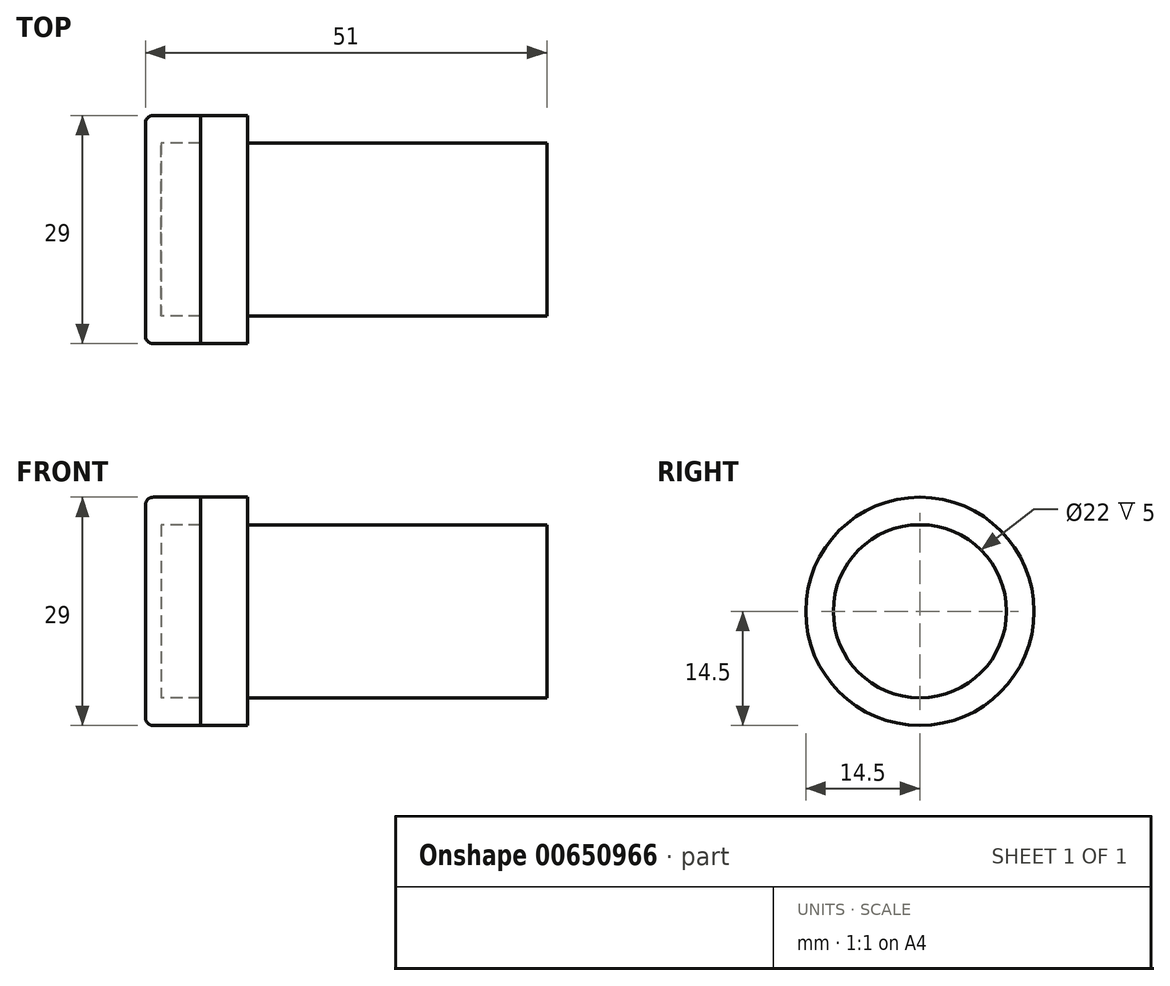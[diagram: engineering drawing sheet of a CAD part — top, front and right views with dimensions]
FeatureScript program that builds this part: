
annotation { "Feature Type Name" : "Feature", "Feature Type Description" : "" }
export const myFeature = defineFeature(function(context is Context, id is Id, definition is map)
    precondition{}
    {
        {
            var Q0;
            Q0=qCreatedBy(makeId("Top.planeOp"),FACE);
            var sketch = newSketch(context, id + "F0", { "sketchPlane" : qUnion([Q0])});
            skLineSegment(sketch, "E0", {"start": v(51, 0) * mm, "end": v(51, 11) * mm});
            skLineSegment(sketch, "E1", {"start": v(51, 11) * mm, "end": v(13, 11) * mm});
            skLineSegment(sketch, "E2", {"start": v(13, 11) * mm, "end": v(13, 14.5) * mm});
            skLineSegment(sketch, "E3", {"start": v(13, 14.5) * mm, "end": v(7, 14.5) * mm});
            skLineSegment(sketch, "E4", {"start": v(7, 14.5) * mm, "end": v(7, 11) * mm});
            skLineSegment(sketch, "E5", {"start": v(0, 11) * mm, "end": v(0, 0) * mm});
            skLineSegment(sketch, "E6", {"start": v(0, 11) * mm, "end": v(0, 14.5) * mm});
            skLineSegment(sketch, "E7", {"start": v(0, 14.5) * mm, "end": v(7, 14.5) * mm});
            skLineSegment(sketch, "E8", {"start": v(2, 0) * mm, "end": v(2, 11) * mm});
            skLineSegment(sketch, "E9", {"start": v(0, 11) * mm, "end": v(2, 11) * mm});
            skLineSegment(sketch, "E10", {"start": v(2, 11) * mm, "end": v(7, 11) * mm});
            skLineSegment(sketch, "E11", {"start": v(7, 11) * mm, "end": v(7, 0) * mm});
            skLineSegment(sketch, "E12", {"start": v(0, 0) * mm, "end": v(7, 0) * mm});
            skLineSegment(sketch, "E13", {"start": v(7, 0) * mm, "end": v(51, 0) * mm});
            skSolve(sketch);
        }
        {
            var Q0;
            {var subQ0=sQuery(id+"F0.wireOp",EDGE,"E8");Q0=makeQuery(id+"F0.imprint","IMPRINT",FACE,{"disambiguationData":[TD([[makeQuery(id+"F0.imprint","IMPRINT",EDGE,{"derivedFrom":subQ0}),-1.0]])]});}
            var Q1;
            Q1=makeQuery(id+"F0.imprint","IMPRINT",FACE,{"disambiguationData":[TD([[makeQuery(id+"F0.imprint","IMPRINT",EDGE,{"derivedFrom":sQuery(id+"F0.wireOp",EDGE,"E0")}),1.0]])]});
            var Q2;
            Q2=sQuery(id+"F0.wireOp",EDGE,"E8");
            var Q3;
            Q3=sQuery(id+"F0.wireOp",EDGE,"E10");
            var Q4;
            Q4=sQuery(id+"F0.wireOp",EDGE,"E4");
            var Q5;
            Q5=sQuery(id+"F0.wireOp",EDGE,"E3");
            var Q6;
            Q6=sQuery(id+"F0.wireOp",EDGE,"E2");
            var Q7;
            Q7=sQuery(id+"F0.wireOp",EDGE,"E1");
            var Q8;
            Q8=sQuery(id+"F0.wireOp",EDGE,"E0");
            var Q9;
            Q9=sQuery(id+"F0.wireOp",EDGE,"E13");
            revolve(context, id + "F1", {"surfaceOperationType" : NewSurfaceOperationType.NEW, "entities" : qUnion([Q0, Q1]), "surfaceEntities" : qUnion([Q2, Q3, Q4, Q5, Q6, Q7, Q8]), "axis" : qUnion([Q9]), "revolveType" : RevolveType.FULL});
        }
        {
            var Q0;
            Q0=makeQuery(id+"F0.imprint","IMPRINT",FACE,{"disambiguationData":[TD([[makeQuery(id+"F0.imprint","IMPRINT",EDGE,{"derivedFrom":sQuery(id+"F0.wireOp",EDGE,"E4")}),-1.0]])]});
            var Q1;
            {var subQ0=sQuery(id+"F0.wireOp",EDGE,"E5");Q1=makeQuery(id+"F0.imprint","IMPRINT",FACE,{"disambiguationData":[TD([[makeQuery(id+"F0.imprint","IMPRINT",EDGE,{"derivedFrom":subQ0}),1.0]])]});}
            var Q2;
            Q2=sQuery(id+"F0.wireOp",EDGE,"E4");
            var Q3;
            Q3=sQuery(id+"F0.wireOp",EDGE,"E7");
            var Q4;
            Q4=sQuery(id+"F0.wireOp",EDGE,"E6");
            var Q5;
            Q5=sQuery(id+"F0.wireOp",EDGE,"E5");
            var Q6;
            Q6=sQuery(id+"F0.wireOp",EDGE,"E8");
            var Q7;
            Q7=sQuery(id+"F0.wireOp",EDGE,"E10");
            var Q8;
            Q8=sQuery(id+"F0.wireOp",EDGE,"E12");
            revolve(context, id + "F2", {"surfaceOperationType" : NewSurfaceOperationType.NEW, "entities" : qUnion([Q0, Q1]), "surfaceEntities" : qUnion([Q2, Q3, Q4, Q5, Q6, Q7]), "axis" : qUnion([Q8]), "revolveType" : RevolveType.FULL});
        }
        {
            var Q0;
            Q0=makeQuery(id+"F2.opRevolve","SWEPT_EDGE",EDGE,{"disambiguationData":[OSD([sQuery(id+"F0.wireOp",EDGE,"E6"),sQuery(id+"F0.wireOp",EDGE,"E7")])]});
            fillet(context, id + "F3", {"entities" : qUnion([Q0]), "radius" : 1 * mm, "tangentPropagation" : true, "allowEdgeOverflow" : false});
        }
    });
